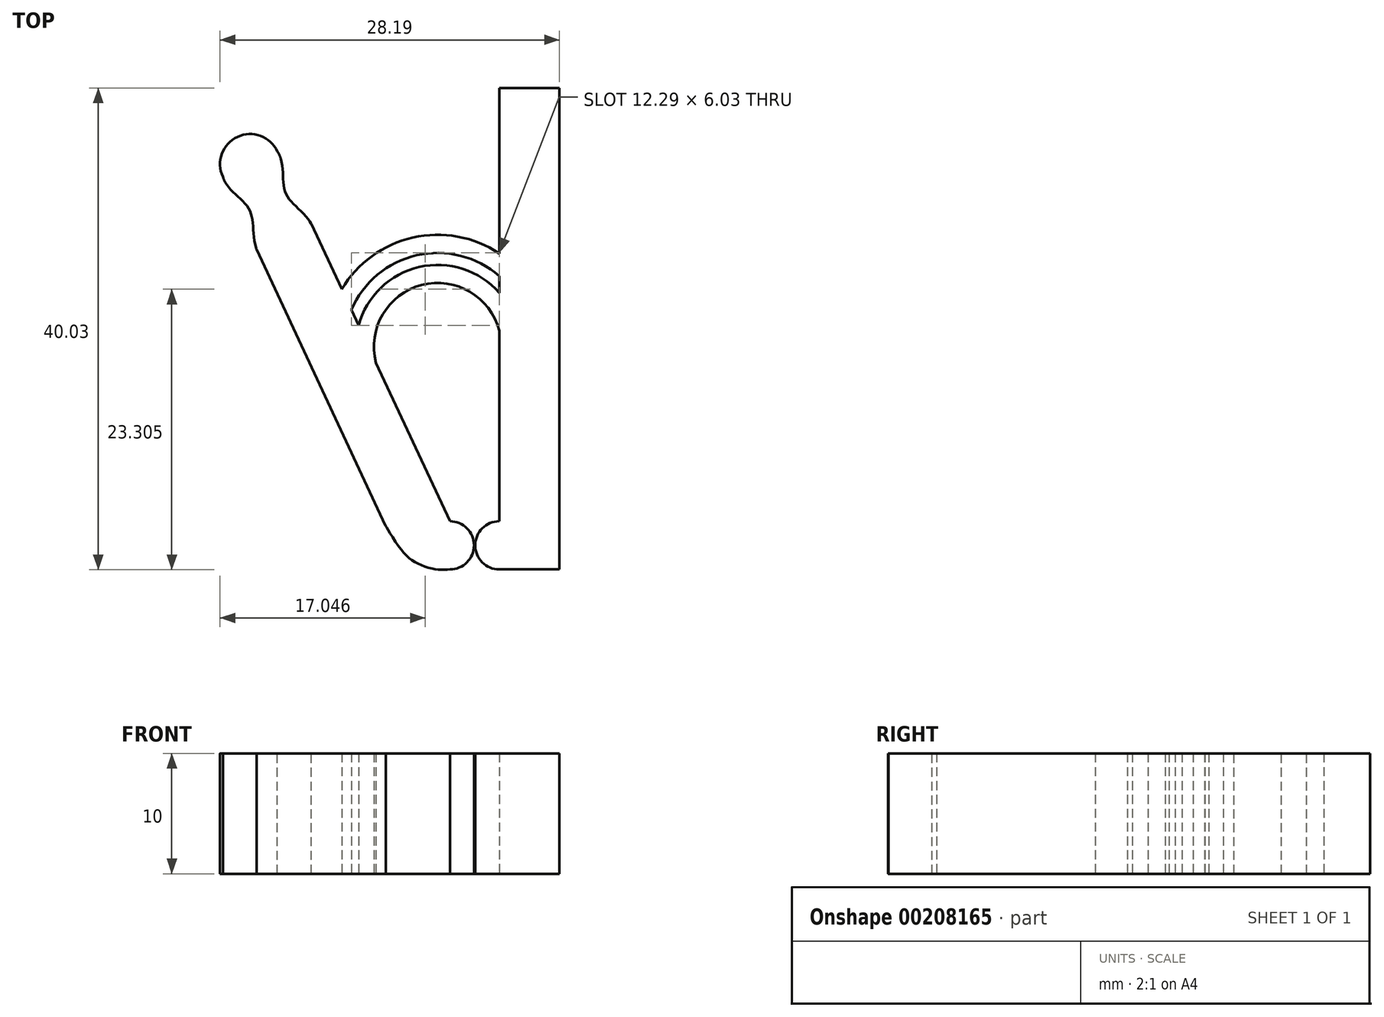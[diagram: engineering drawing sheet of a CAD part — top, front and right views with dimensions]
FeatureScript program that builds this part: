
annotation { "Feature Type Name" : "Feature", "Feature Type Description" : "" }
export const myFeature = defineFeature(function(context is Context, id is Id, definition is map)
    precondition{}
    {
        {
            var Q0;
            Q0=qCreatedBy(makeId("Top.planeOp"),FACE);
            var sketch = newSketch(context, id + "F0", { "sketchPlane" : qUnion([Q0])});
            skLineSegment(sketch, "E0.top", {"start": v(0, -50) * mm, "end": v(5, -50) * mm});
            skLineSegment(sketch, "E0.left", {"start": v(0, -10) * mm, "end": v(0, -23.75) * mm});
            skLineSegment(sketch, "E0.right", {"start": v(5, -10) * mm, "end": v(5, -50) * mm});
            skLineSegment(sketch, "E1", {"start": v(0, -50) * mm, "end": v(-4.1, -50) * mm, "construction": true});
            skLineSegment(sketch, "E2", {"start": v(-9.43, -46.4) * mm, "end": v(-20.17, -23.36) * mm});
            skLineSegment(sketch, "E3", {"start": v(0, -10) * mm, "end": v(-28.85, -10) * mm, "construction": true});
            skArc(sketch, "E4", {"start": v(0, -46) * mm, "mid": v(-2, -48) * mm, "end": v(0, -50) * mm});
            skLineSegment(sketch, "E5", {"start": v(-4.1, -50) * mm, "end": v(-4.1, -46) * mm});
            skArc(sketch, "E6", {"start": v(-4.1, -50) * mm, "mid": v(-2.1, -48) * mm, "end": v(-4.1, -46) * mm});
            skLineSegment(sketch, "E7.0", {"start": v(-4.1, -46) * mm, "end": v(-10.24, -32.83) * mm});
            skLineSegment(sketch, "E8", {"start": v(-20.47, -16.81) * mm, "end": v(-19.56, -18.77) * mm});
            skFitSpline(sketch, "E9", {"points": [v(-4.1, -50) * mm, v(-5.23, -50) * mm, v(-6.89, -49.45) * mm, v(-8.3, -48.16) * mm, v(-9.43, -46.4) * mm, v(-9.44, -46.38) * mm], "startDerivative": vector(-5.35, -0.43) * mm, "endDerivative": vector(-0.13, 0.35) * mm});
            skArc(sketch, "E10", {"start": v(0, -30.17) * mm, "mid": v(-6.45, -26.38) * mm, "end": v(-10.24, -32.83) * mm});
            skArc(sketch, "E11.0", {"start": v(0, -27.04) * mm, "mid": v(-6.65, -24.88) * mm, "end": v(-11.68, -29.74) * mm});
            skLineSegment(sketch, "E12.trimOffspring", {"start": v(-11.68, -29.74) * mm, "end": v(-12.29, -28.44) * mm});
            skLineSegment(sketch, "E13.trimOffspring", {"start": v(0, -30.17) * mm, "end": v(0, -50) * mm});
            skArc(sketch, "E14", {"start": v(-18.43, -15.28) * mm, "mid": v(-21.75, -14.07) * mm, "end": v(-22.96, -17.39) * mm});
            skArc(sketch, "E15.0", {"start": v(0, -25.63) * mm, "mid": v(-6.86, -23.9) * mm, "end": v(-12.29, -28.44) * mm});
            skArc(sketch, "E16.0", {"start": v(0, -23.75) * mm, "mid": v(-7.18, -22.44) * mm, "end": v(-13.09, -26.72) * mm});
            skLineSegment(sketch, "E17.trimOffspring", {"start": v(0, -25.63) * mm, "end": v(0, -27.04) * mm});
            skLineSegment(sketch, "E18.trimOffspring", {"start": v(-13.09, -26.72) * mm, "end": v(-15.64, -21.25) * mm});
            skFitSpline(sketch, "E19", {"points": [v(-22.96, -17.39) * mm, v(-22.15, -18.63) * mm, v(-21.3, -19.4) * mm, v(-20.72, -20.2) * mm, v(-20.48, -21.14) * mm, v(-20.36, -22.48) * mm, v(-20.17, -23.36) * mm, v(-20.13, -23.44) * mm], "startDerivative": vector(2.84, -8.62) * mm, "endDerivative": vector(0.43, -1.3) * mm});
            skFitSpline(sketch, "E20.MirrorCS", {"points": [v(-18.43, -15.28) * mm, v(-18, -16.7) * mm, v(-17.95, -17.85) * mm, v(-17.71, -18.8) * mm, v(-17.14, -19.59) * mm, v(-16.2, -20.53) * mm, v(-15.64, -21.25) * mm, v(-15.6, -21.33) * mm], "startDerivative": vector(4.78, -7.72) * mm, "endDerivative": vector(0.72, -1.16) * mm});
            skLineSegment(sketch, "E21.trimOffspring", {"start": v(-22.7, -17.96) * mm, "end": v(-22.96, -17.39) * mm});
            skLineSegment(sketch, "E22.trimOffspring", {"start": v(-18.16, -15.85) * mm, "end": v(-18.43, -15.28) * mm});
            skLineSegment(sketch, "E23", {"start": v(0, -10) * mm, "end": v(5, -10) * mm});
            skSolve(sketch);
        }
        {
            var Q0;
            Q0 = qSketchRegion(id + "F0", true);
            extrude(context, id + "F1", {"entities" : qUnion([Q0]), "depth" : 10 * mm});
        }
    });
